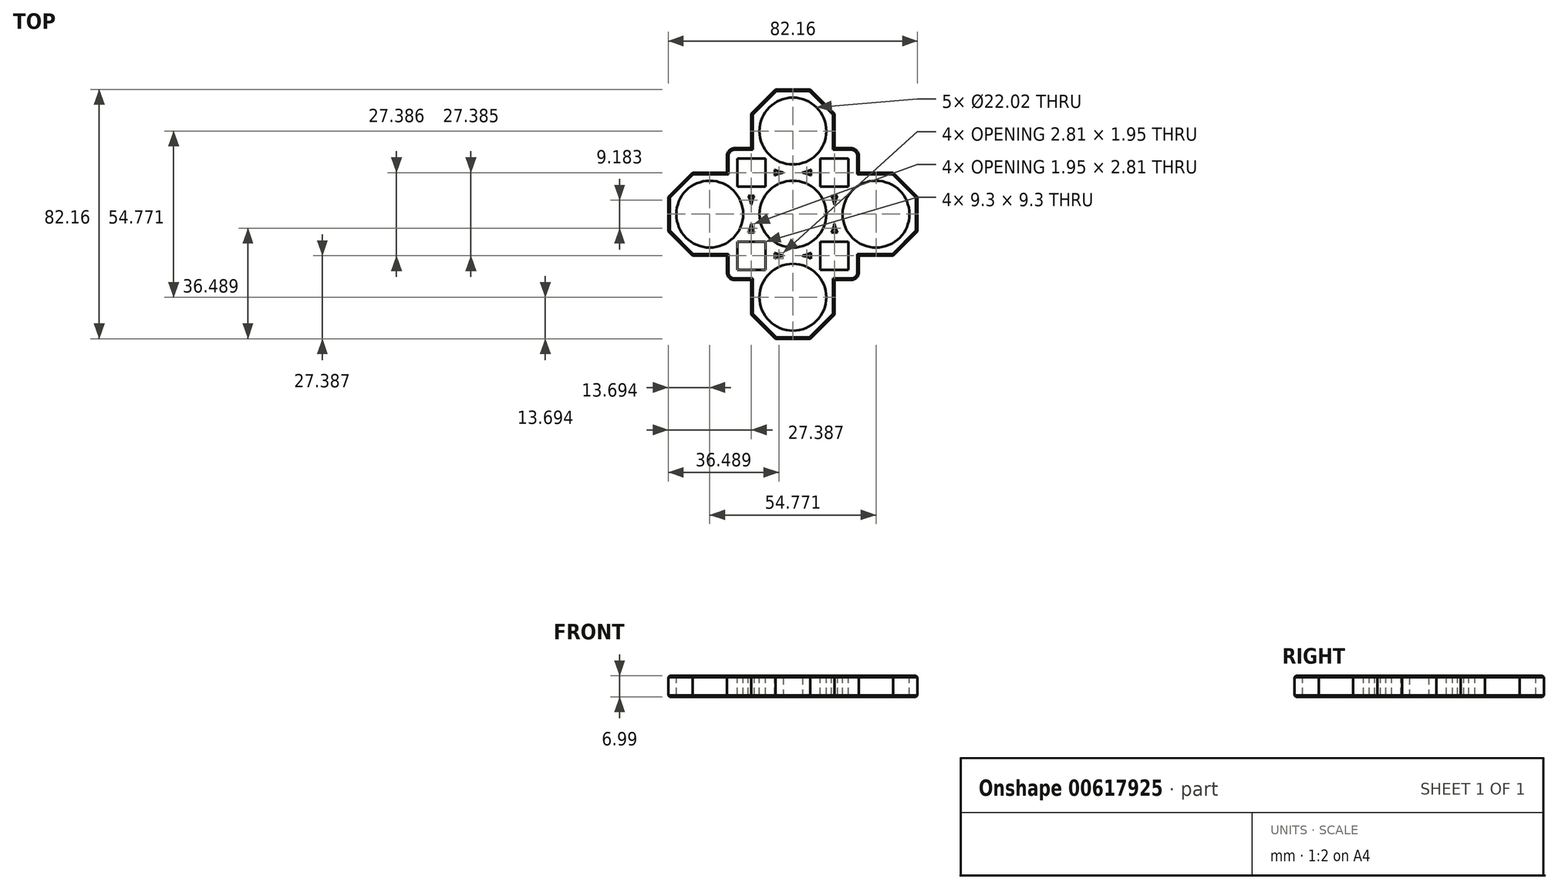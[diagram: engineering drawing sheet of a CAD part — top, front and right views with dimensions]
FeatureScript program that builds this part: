
annotation { "Feature Type Name" : "Feature", "Feature Type Description" : "" }
export const myFeature = defineFeature(function(context is Context, id is Id, definition is map)
    precondition{}
    {
        {
            var Q0;
            Q0=qCreatedBy(makeId("Top.planeOp"),FACE);
            var sketch = newSketch(context, id + "F0", { "sketchPlane" : qUnion([Q0])});
            skCircle(sketch, "E0", {"center": v(-27.39, 0) * mm, "radius": 11.01 * mm});
            skCircle(sketch, "E1.cCircle", {"center": v(-27.39, 0) * mm, "radius": 14.82 * mm, "construction": true});
            skLineSegment(sketch, "E1.0", {"start": v(-13.7, -5.67) * mm, "end": v(-21.71, -13.7) * mm});
            skLineSegment(sketch, "E1.1", {"start": v(-21.71, -13.7) * mm, "end": v(-33.06, -13.7) * mm});
            skLineSegment(sketch, "E1.2", {"start": v(-33.06, -13.7) * mm, "end": v(-41.08, -5.67) * mm});
            skLineSegment(sketch, "E1.3", {"start": v(-41.08, -5.67) * mm, "end": v(-41.08, 5.67) * mm});
            skLineSegment(sketch, "E1.4", {"start": v(-41.08, 5.67) * mm, "end": v(-33.06, 13.7) * mm});
            skLineSegment(sketch, "E1.5", {"start": v(-33.06, 13.7) * mm, "end": v(-21.71, 13.7) * mm});
            skLineSegment(sketch, "E1.6", {"start": v(-21.71, 13.7) * mm, "end": v(-13.7, 5.67) * mm});
            skLineSegment(sketch, "E1.7", {"start": v(-13.7, 5.67) * mm, "end": v(-13.7, -5.67) * mm});
            skCircle(sketch, "E2", {"center": v(0, -27.39) * mm, "radius": 11.01 * mm});
            skCircle(sketch, "E3.cCircle", {"center": v(0, -27.39) * mm, "radius": 14.82 * mm, "construction": true});
            skLineSegment(sketch, "E3.0", {"start": v(13.7, -33.06) * mm, "end": v(5.67, -41.08) * mm});
            skLineSegment(sketch, "E3.1", {"start": v(5.67, -41.08) * mm, "end": v(-5.67, -41.08) * mm});
            skLineSegment(sketch, "E3.2", {"start": v(-5.67, -41.08) * mm, "end": v(-13.7, -33.06) * mm});
            skLineSegment(sketch, "E3.3", {"start": v(-13.7, -33.06) * mm, "end": v(-13.7, -21.71) * mm});
            skLineSegment(sketch, "E3.4", {"start": v(-13.7, -21.71) * mm, "end": v(-5.67, -13.7) * mm});
            skLineSegment(sketch, "E3.5", {"start": v(-5.67, -13.7) * mm, "end": v(5.67, -13.7) * mm});
            skLineSegment(sketch, "E3.6", {"start": v(5.67, -13.7) * mm, "end": v(13.7, -21.71) * mm});
            skLineSegment(sketch, "E3.7", {"start": v(13.7, -21.71) * mm, "end": v(13.7, -33.06) * mm});
            skCircle(sketch, "E4", {"center": v(27.39, 0) * mm, "radius": 11.01 * mm});
            skCircle(sketch, "E5.cCircle", {"center": v(27.39, 0) * mm, "radius": 14.82 * mm, "construction": true});
            skLineSegment(sketch, "E5.0", {"start": v(41.08, -5.67) * mm, "end": v(33.06, -13.7) * mm});
            skLineSegment(sketch, "E5.1", {"start": v(33.06, -13.7) * mm, "end": v(21.71, -13.7) * mm});
            skLineSegment(sketch, "E5.2", {"start": v(21.71, -13.7) * mm, "end": v(13.7, -5.67) * mm});
            skLineSegment(sketch, "E5.3", {"start": v(13.7, -5.67) * mm, "end": v(13.7, 5.67) * mm});
            skLineSegment(sketch, "E5.4", {"start": v(13.7, 5.67) * mm, "end": v(21.71, 13.7) * mm});
            skLineSegment(sketch, "E5.5", {"start": v(21.71, 13.7) * mm, "end": v(33.06, 13.7) * mm});
            skLineSegment(sketch, "E5.6", {"start": v(33.06, 13.7) * mm, "end": v(41.08, 5.67) * mm});
            skLineSegment(sketch, "E5.7", {"start": v(41.08, 5.67) * mm, "end": v(41.08, -5.67) * mm});
            skCircle(sketch, "E6", {"center": v(0, 27.39) * mm, "radius": 11.01 * mm});
            skCircle(sketch, "E7.cCircle", {"center": v(0, 27.39) * mm, "radius": 14.82 * mm, "construction": true});
            skLineSegment(sketch, "E7.0", {"start": v(13.7, 21.71) * mm, "end": v(5.67, 13.7) * mm});
            skLineSegment(sketch, "E7.1", {"start": v(5.67, 13.7) * mm, "end": v(-5.67, 13.7) * mm});
            skLineSegment(sketch, "E7.2", {"start": v(-5.67, 13.7) * mm, "end": v(-13.7, 21.71) * mm});
            skLineSegment(sketch, "E7.3", {"start": v(-13.7, 21.71) * mm, "end": v(-13.7, 33.06) * mm});
            skLineSegment(sketch, "E7.4", {"start": v(-13.7, 33.06) * mm, "end": v(-5.67, 41.08) * mm});
            skLineSegment(sketch, "E7.5", {"start": v(-5.67, 41.08) * mm, "end": v(5.67, 41.08) * mm});
            skLineSegment(sketch, "E7.6", {"start": v(5.67, 41.08) * mm, "end": v(13.7, 33.06) * mm});
            skLineSegment(sketch, "E7.7", {"start": v(13.7, 33.06) * mm, "end": v(13.7, 21.71) * mm});
            skCircle(sketch, "E8", {"center": v(0, 0) * mm, "radius": 11.01 * mm});
            skCircle(sketch, "E9.cCircle", {"center": v(0, 0) * mm, "radius": 14.82 * mm, "construction": true});
            skLineSegment(sketch, "E9.1", {"start": v(5.67, -13.7) * mm, "end": v(-5.67, -13.7) * mm});
            skLineSegment(sketch, "E9.3", {"start": v(-13.7, -5.67) * mm, "end": v(-13.7, 5.67) * mm});
            skLineSegment(sketch, "E9.5", {"start": v(-5.67, 13.7) * mm, "end": v(5.67, 13.7) * mm});
            skLineSegment(sketch, "E9.7", {"start": v(13.7, 5.67) * mm, "end": v(13.7, -5.67) * mm});
            skLineSegment(sketch, "E10.bottom", {"start": v(-13.7, 21.71) * mm, "end": v(-21.71, 21.71) * mm});
            skLineSegment(sketch, "E10.right", {"start": v(-21.71, 21.71) * mm, "end": v(-21.71, 13.7) * mm});
            skLineSegment(sketch, "E11.top", {"start": v(-21.71, -21.71) * mm, "end": v(-13.7, -21.71) * mm});
            skLineSegment(sketch, "E11.left", {"start": v(-21.71, -13.7) * mm, "end": v(-21.71, -21.71) * mm});
            skLineSegment(sketch, "E12.top", {"start": v(21.71, -21.71) * mm, "end": v(13.7, -21.71) * mm});
            skLineSegment(sketch, "E12.left", {"start": v(21.71, -13.7) * mm, "end": v(21.71, -21.71) * mm});
            skLineSegment(sketch, "E13.bottom", {"start": v(13.7, 21.71) * mm, "end": v(21.71, 21.71) * mm});
            skLineSegment(sketch, "E13.right", {"start": v(21.71, 21.71) * mm, "end": v(21.71, 13.7) * mm});
            skSolve(sketch);
        }
        {
            var Q0;
            Q0 = qSketchRegion(id + "F0", true);
            extrude(context, id + "F1", {"entities" : qUnion([Q0]), "oppositeDirection" : true, "depth" : 7 * mm, "offsetDistance" : 25.4 * mm});
        }
        {
            var Q0;
            Q0=qCreatedBy(makeId("Top.planeOp"),FACE);
            var sketch = newSketch(context, id + "F2", { "sketchPlane" : qUnion([Q0])});
            skCircle(sketch, "E14.cCircle", {"center": v(-13.7, 13.7) * mm, "radius": 4.65 * mm, "construction": true});
            skLineSegment(sketch, "E14.0", {"start": v(-18.34, 18.34) * mm, "end": v(-9.04, 18.34) * mm});
            skLineSegment(sketch, "E14.1", {"start": v(-9.04, 18.34) * mm, "end": v(-9.04, 9.04) * mm});
            skLineSegment(sketch, "E14.2", {"start": v(-9.04, 9.04) * mm, "end": v(-18.34, 9.04) * mm});
            skLineSegment(sketch, "E14.3", {"start": v(-18.34, 9.04) * mm, "end": v(-18.34, 18.34) * mm});
            skPoint(sketch, "E14.0.midPoint", {"position": v(-13.7, 18.34) * mm});
            skPoint(sketch, "E15.MirrorP", {"position": v(13.7, 18.34) * mm});
            skLineSegment(sketch, "E16.MirrorCS", {"start": v(18.34, 18.34) * mm, "end": v(9.04, 18.34) * mm});
            skLineSegment(sketch, "E17.MirrorCS", {"start": v(18.34, 9.04) * mm, "end": v(18.34, 18.34) * mm});
            skCircle(sketch, "E18.MirrorC", {"center": v(13.7, 13.7) * mm, "radius": 4.65 * mm, "construction": true});
            skLineSegment(sketch, "E19.MirrorCS", {"start": v(9.04, 9.04) * mm, "end": v(18.34, 9.04) * mm});
            skLineSegment(sketch, "E20.MirrorCS", {"start": v(9.04, 18.34) * mm, "end": v(9.04, 9.04) * mm});
            skLineSegment(sketch, "E21.MirrorCS", {"start": v(18.34, -9.04) * mm, "end": v(18.34, -18.34) * mm});
            skLineSegment(sketch, "E22.MirrorCS", {"start": v(-18.34, -9.04) * mm, "end": v(-18.34, -18.34) * mm});
            skLineSegment(sketch, "E23.MirrorCS", {"start": v(-9.04, -9.04) * mm, "end": v(-18.34, -9.04) * mm});
            skLineSegment(sketch, "E24.MirrorCS", {"start": v(-9.04, -18.34) * mm, "end": v(-9.04, -9.04) * mm});
            skLineSegment(sketch, "E25.MirrorCS", {"start": v(9.04, -9.04) * mm, "end": v(18.34, -9.04) * mm});
            skLineSegment(sketch, "E26.MirrorCS", {"start": v(-18.34, -18.34) * mm, "end": v(-9.04, -18.34) * mm});
            skLineSegment(sketch, "E27.MirrorCS", {"start": v(9.04, -18.34) * mm, "end": v(9.04, -9.04) * mm});
            skLineSegment(sketch, "E28.MirrorCS", {"start": v(18.34, -18.34) * mm, "end": v(9.04, -18.34) * mm});
            skCircle(sketch, "E29.MirrorC", {"center": v(13.7, -13.7) * mm, "radius": 4.65 * mm, "construction": true});
            skCircle(sketch, "E30.MirrorC", {"center": v(-13.7, -13.7) * mm, "radius": 4.65 * mm, "construction": true});
            skPoint(sketch, "E31.MirrorP", {"position": v(-13.7, -18.34) * mm});
            skPoint(sketch, "E32.MirrorP", {"position": v(13.7, -18.34) * mm});
            skSolve(sketch);
        }
        {
            var Q0;
            Q0 = qSketchRegion(id + "F2", true);
            extrude(context, id + "F3", {"entities" : qUnion([Q0]), "operationType" : NewBodyOperationType.REMOVE, "oppositeDirection" : true, "depth" : 25.4 * mm, "offsetDistance" : 25.4 * mm});
        }
        {
            var Q0;
            Q0=makeQuery(id+"F1.opExtrude","SWEPT_EDGE",EDGE,{"disambiguationData":[OSD([sQuery(id+"F0.wireOp",EDGE,"E10.bottom"),sQuery(id+"F0.wireOp",EDGE,"E10.right")])]});
            var Q1;
            Q1=makeQuery(id+"F1.opExtrude","SWEPT_EDGE",EDGE,{"disambiguationData":[OSD([sQuery(id+"F0.wireOp",EDGE,"E13.bottom"),sQuery(id+"F0.wireOp",EDGE,"E13.right")])]});
            var Q2;
            Q2=makeQuery(id+"F1.opExtrude","SWEPT_EDGE",EDGE,{"disambiguationData":[OSD([sQuery(id+"F0.wireOp",EDGE,"E12.top"),sQuery(id+"F0.wireOp",EDGE,"E12.left")])]});
            var Q3;
            Q3=makeQuery(id+"F1.opExtrude","SWEPT_EDGE",EDGE,{"disambiguationData":[OSD([sQuery(id+"F0.wireOp",EDGE,"E11.top"),sQuery(id+"F0.wireOp",EDGE,"E11.left")])]});
            fillet(context, id + "F4", {"entities" : qUnion([Q0, Q1, Q2, Q3]), "radius" : 2.54 * mm, "tangentPropagation" : true, "allowEdgeOverflow" : false});
        }
        {
            var Q0;
            Q0=makeQuery(id+"F1.opExtrude","CAP_EDGE",EDGE,{"disambiguationData":[OSD([sQuery(id+"F0.wireOp",EDGE,"E5.7")])],"isStart":false});
            var Q1;
            Q1=makeQuery(id+"F1.opExtrude","CAP_EDGE",EDGE,{"disambiguationData":[OSD([sQuery(id+"F0.wireOp",EDGE,"E5.6")])],"isStart":false});
            var Q2;
            Q2=makeQuery(id+"F1.opExtrude","CAP_EDGE",EDGE,{"disambiguationData":[OSD([sQuery(id+"F0.wireOp",EDGE,"E5.5")])],"isStart":false});
            var Q3;
            Q3=makeQuery(id+"F1.opExtrude","CAP_EDGE",EDGE,{"disambiguationData":[OSD([sQuery(id+"F0.wireOp",EDGE,"E13.right")])],"isStart":false});
            var Q4;
            Q4=makeQuery(id+"F1.opExtrude","CAP_EDGE",EDGE,{"disambiguationData":[OSD([sQuery(id+"F0.wireOp",EDGE,"E13.bottom")])],"isStart":false});
            var Q5;
            Q5=makeQuery(id+"F1.opExtrude","CAP_EDGE",EDGE,{"disambiguationData":[OSD([sQuery(id+"F0.wireOp",EDGE,"E7.7")])],"isStart":false});
            var Q6;
            Q6=makeQuery(id+"F1.opExtrude","CAP_EDGE",EDGE,{"disambiguationData":[OSD([sQuery(id+"F0.wireOp",EDGE,"E7.6")])],"isStart":false});
            var Q7;
            Q7=makeQuery(id+"F1.opExtrude","CAP_EDGE",EDGE,{"disambiguationData":[OSD([sQuery(id+"F0.wireOp",EDGE,"E7.5")])],"isStart":false});
            var Q8;
            Q8=makeQuery(id+"F1.opExtrude","CAP_EDGE",EDGE,{"disambiguationData":[OSD([sQuery(id+"F0.wireOp",EDGE,"E7.4")])],"isStart":false});
            var Q9;
            Q9=makeQuery(id+"F1.opExtrude","CAP_EDGE",EDGE,{"disambiguationData":[OSD([sQuery(id+"F0.wireOp",EDGE,"E7.3")])],"isStart":false});
            var Q10;
            Q10=makeQuery(id+"F1.opExtrude","CAP_EDGE",EDGE,{"disambiguationData":[OSD([sQuery(id+"F0.wireOp",EDGE,"E10.bottom")])],"isStart":false});
            var Q11;
            Q11=makeQuery(id+"F1.opExtrude","CAP_EDGE",EDGE,{"disambiguationData":[OSD([sQuery(id+"F0.wireOp",EDGE,"E5.0")])],"isStart":false});
            var Q12;
            Q12=makeQuery(id+"F1.opExtrude","CAP_EDGE",EDGE,{"disambiguationData":[OSD([sQuery(id+"F0.wireOp",EDGE,"E5.1")])],"isStart":false});
            var Q13;
            Q13=makeQuery(id+"F1.opExtrude","CAP_EDGE",EDGE,{"disambiguationData":[OSD([sQuery(id+"F0.wireOp",EDGE,"E12.left")])],"isStart":false});
            var Q14;
            Q14=makeQuery(id+"F1.opExtrude","CAP_EDGE",EDGE,{"disambiguationData":[OSD([sQuery(id+"F0.wireOp",EDGE,"E12.top")])],"isStart":false});
            var Q15;
            Q15=makeQuery(id+"F1.opExtrude","CAP_EDGE",EDGE,{"disambiguationData":[OSD([sQuery(id+"F0.wireOp",EDGE,"E3.7")])],"isStart":false});
            var Q16;
            Q16=makeQuery(id+"F1.opExtrude","CAP_EDGE",EDGE,{"disambiguationData":[OSD([sQuery(id+"F0.wireOp",EDGE,"E3.0")])],"isStart":false});
            var Q17;
            Q17=makeQuery(id+"F1.opExtrude","CAP_EDGE",EDGE,{"disambiguationData":[OSD([sQuery(id+"F0.wireOp",EDGE,"E3.1")])],"isStart":false});
            var Q18;
            Q18=makeQuery(id+"F1.opExtrude","CAP_EDGE",EDGE,{"disambiguationData":[OSD([sQuery(id+"F0.wireOp",EDGE,"E3.2")])],"isStart":false});
            var Q19;
            Q19=makeQuery(id+"F1.opExtrude","CAP_EDGE",EDGE,{"disambiguationData":[OSD([sQuery(id+"F0.wireOp",EDGE,"E3.3")])],"isStart":false});
            var Q20;
            Q20=makeQuery(id+"F1.opExtrude","CAP_EDGE",EDGE,{"disambiguationData":[OSD([sQuery(id+"F0.wireOp",EDGE,"E11.top")])],"isStart":false});
            var Q21;
            Q21=makeQuery(id+"F1.opExtrude","CAP_EDGE",EDGE,{"disambiguationData":[OSD([sQuery(id+"F0.wireOp",EDGE,"E11.left")])],"isStart":false});
            var Q22;
            Q22=makeQuery(id+"F1.opExtrude","CAP_EDGE",EDGE,{"disambiguationData":[OSD([sQuery(id+"F0.wireOp",EDGE,"E1.1")])],"isStart":false});
            var Q23;
            Q23=makeQuery(id+"F1.opExtrude","CAP_EDGE",EDGE,{"disambiguationData":[OSD([sQuery(id+"F0.wireOp",EDGE,"E1.2")])],"isStart":false});
            var Q24;
            Q24=makeQuery(id+"F1.opExtrude","CAP_EDGE",EDGE,{"disambiguationData":[OSD([sQuery(id+"F0.wireOp",EDGE,"E1.3")])],"isStart":false});
            var Q25;
            Q25=makeQuery(id+"F1.opExtrude","CAP_EDGE",EDGE,{"disambiguationData":[OSD([sQuery(id+"F0.wireOp",EDGE,"E1.4")])],"isStart":false});
            var Q26;
            Q26=makeQuery(id+"F1.opExtrude","CAP_EDGE",EDGE,{"disambiguationData":[OSD([sQuery(id+"F0.wireOp",EDGE,"E1.5")])],"isStart":false});
            var Q27;
            Q27=makeQuery(id+"F1.opExtrude","CAP_EDGE",EDGE,{"disambiguationData":[OSD([sQuery(id+"F0.wireOp",EDGE,"E10.right")])],"isStart":false});
            chamfer(context, id + "F5", {"entities" : qUnion([Q0, Q1, Q2, Q3, Q4, Q5, Q6, Q7, Q8, Q9, Q10, Q11, Q12, Q13, Q14, Q15, Q16, Q17, Q18, Q19, Q20, Q21, Q22, Q23, Q24, Q25, Q26, Q27]), "width" : 0.5 * mm, "tangentPropagation" : true});
        }
        {
            var Q0;
            Q0=makeQuery(id+"F1.opExtrude","CAP_EDGE",EDGE,{"disambiguationData":[OSD([sQuery(id+"F0.wireOp",EDGE,"E3.0")])],"isStart":true});
            var Q1;
            Q1=makeQuery(id+"F1.opExtrude","CAP_EDGE",EDGE,{"disambiguationData":[OSD([sQuery(id+"F0.wireOp",EDGE,"E3.1")])],"isStart":true});
            var Q2;
            Q2=makeQuery(id+"F1.opExtrude","CAP_EDGE",EDGE,{"disambiguationData":[OSD([sQuery(id+"F0.wireOp",EDGE,"E3.2")])],"isStart":true});
            var Q3;
            Q3=makeQuery(id+"F1.opExtrude","CAP_EDGE",EDGE,{"disambiguationData":[OSD([sQuery(id+"F0.wireOp",EDGE,"E3.3")])],"isStart":true});
            var Q4;
            Q4=makeQuery(id+"F1.opExtrude","CAP_EDGE",EDGE,{"disambiguationData":[OSD([sQuery(id+"F0.wireOp",EDGE,"E11.top")])],"isStart":true});
            var Q5;
            Q5=makeQuery(id+"F1.opExtrude","CAP_EDGE",EDGE,{"disambiguationData":[OSD([sQuery(id+"F0.wireOp",EDGE,"E11.left")])],"isStart":true});
            var Q6;
            Q6=makeQuery(id+"F1.opExtrude","CAP_EDGE",EDGE,{"disambiguationData":[OSD([sQuery(id+"F0.wireOp",EDGE,"E1.1")])],"isStart":true});
            var Q7;
            Q7=makeQuery(id+"F1.opExtrude","CAP_EDGE",EDGE,{"disambiguationData":[OSD([sQuery(id+"F0.wireOp",EDGE,"E1.2")])],"isStart":true});
            var Q8;
            Q8=makeQuery(id+"F1.opExtrude","CAP_EDGE",EDGE,{"disambiguationData":[OSD([sQuery(id+"F0.wireOp",EDGE,"E1.5")])],"isStart":true});
            var Q9;
            Q9=makeQuery(id+"F1.opExtrude","CAP_EDGE",EDGE,{"disambiguationData":[OSD([sQuery(id+"F0.wireOp",EDGE,"E1.4")])],"isStart":true});
            var Q10;
            Q10=makeQuery(id+"F1.opExtrude","CAP_EDGE",EDGE,{"disambiguationData":[OSD([sQuery(id+"F0.wireOp",EDGE,"E1.3")])],"isStart":true});
            var Q11;
            Q11=makeQuery(id+"F1.opExtrude","CAP_EDGE",EDGE,{"disambiguationData":[OSD([sQuery(id+"F0.wireOp",EDGE,"E10.right")])],"isStart":true});
            var Q12;
            Q12=makeQuery(id+"F1.opExtrude","CAP_EDGE",EDGE,{"disambiguationData":[OSD([sQuery(id+"F0.wireOp",EDGE,"E10.bottom")])],"isStart":true});
            var Q13;
            Q13=makeQuery(id+"F1.opExtrude","CAP_EDGE",EDGE,{"disambiguationData":[OSD([sQuery(id+"F0.wireOp",EDGE,"E7.3")])],"isStart":true});
            var Q14;
            Q14=makeQuery(id+"F1.opExtrude","CAP_EDGE",EDGE,{"disambiguationData":[OSD([sQuery(id+"F0.wireOp",EDGE,"E7.4")])],"isStart":true});
            var Q15;
            Q15=makeQuery(id+"F1.opExtrude","CAP_EDGE",EDGE,{"disambiguationData":[OSD([sQuery(id+"F0.wireOp",EDGE,"E7.5")])],"isStart":true});
            var Q16;
            Q16=makeQuery(id+"F1.opExtrude","CAP_EDGE",EDGE,{"disambiguationData":[OSD([sQuery(id+"F0.wireOp",EDGE,"E7.6")])],"isStart":true});
            var Q17;
            Q17=makeQuery(id+"F1.opExtrude","CAP_EDGE",EDGE,{"disambiguationData":[OSD([sQuery(id+"F0.wireOp",EDGE,"E7.7")])],"isStart":true});
            var Q18;
            Q18=makeQuery(id+"F1.opExtrude","CAP_EDGE",EDGE,{"disambiguationData":[OSD([sQuery(id+"F0.wireOp",EDGE,"E13.bottom")])],"isStart":true});
            var Q19;
            Q19=makeQuery(id+"F1.opExtrude","CAP_EDGE",EDGE,{"disambiguationData":[OSD([sQuery(id+"F0.wireOp",EDGE,"E13.right")])],"isStart":true});
            var Q20;
            Q20=makeQuery(id+"F1.opExtrude","CAP_EDGE",EDGE,{"disambiguationData":[OSD([sQuery(id+"F0.wireOp",EDGE,"E5.5")])],"isStart":true});
            var Q21;
            Q21=makeQuery(id+"F1.opExtrude","CAP_EDGE",EDGE,{"disambiguationData":[OSD([sQuery(id+"F0.wireOp",EDGE,"E5.6")])],"isStart":true});
            var Q22;
            Q22=makeQuery(id+"F1.opExtrude","CAP_EDGE",EDGE,{"disambiguationData":[OSD([sQuery(id+"F0.wireOp",EDGE,"E5.7")])],"isStart":true});
            var Q23;
            Q23=makeQuery(id+"F1.opExtrude","CAP_EDGE",EDGE,{"disambiguationData":[OSD([sQuery(id+"F0.wireOp",EDGE,"E5.0")])],"isStart":true});
            var Q24;
            Q24=makeQuery(id+"F1.opExtrude","CAP_EDGE",EDGE,{"disambiguationData":[OSD([sQuery(id+"F0.wireOp",EDGE,"E5.1")])],"isStart":true});
            var Q25;
            Q25=makeQuery(id+"F1.opExtrude","CAP_EDGE",EDGE,{"disambiguationData":[OSD([sQuery(id+"F0.wireOp",EDGE,"E12.left")])],"isStart":true});
            var Q26;
            Q26=makeQuery(id+"F1.opExtrude","CAP_EDGE",EDGE,{"disambiguationData":[OSD([sQuery(id+"F0.wireOp",EDGE,"E12.top")])],"isStart":true});
            var Q27;
            Q27=makeQuery(id+"F1.opExtrude","CAP_EDGE",EDGE,{"disambiguationData":[OSD([sQuery(id+"F0.wireOp",EDGE,"E3.7")])],"isStart":true});
            chamfer(context, id + "F6", {"entities" : qUnion([Q0, Q1, Q2, Q3, Q4, Q5, Q6, Q7, Q8, Q9, Q10, Q11, Q12, Q13, Q14, Q15, Q16, Q17, Q18, Q19, Q20, Q21, Q22, Q23, Q24, Q25, Q26, Q27]), "width" : 0.5 * mm, "tangentPropagation" : true});
        }
        {
            var Q0;
            Q0=makeQuery(id+"F1.opExtrude","CAP_FACE",FACE,{"disambiguationData":[OSD([sQuery(id+"F0.wireOp",EDGE,"E0"),sQuery(id+"F0.wireOp",EDGE,"E1.1"),sQuery(id+"F0.wireOp",EDGE,"E1.2"),sQuery(id+"F0.wireOp",EDGE,"E1.3"),sQuery(id+"F0.wireOp",EDGE,"E1.4"),sQuery(id+"F0.wireOp",EDGE,"E1.5"),sQuery(id+"F0.wireOp",EDGE,"E2"),sQuery(id+"F0.wireOp",EDGE,"E3.0"),sQuery(id+"F0.wireOp",EDGE,"E3.1"),sQuery(id+"F0.wireOp",EDGE,"E3.2"),sQuery(id+"F0.wireOp",EDGE,"E3.3"),sQuery(id+"F0.wireOp",EDGE,"E3.7"),sQuery(id+"F0.wireOp",EDGE,"E4"),sQuery(id+"F0.wireOp",EDGE,"E5.0"),sQuery(id+"F0.wireOp",EDGE,"E5.1"),sQuery(id+"F0.wireOp",EDGE,"E5.5"),sQuery(id+"F0.wireOp",EDGE,"E5.6"),sQuery(id+"F0.wireOp",EDGE,"E5.7"),sQuery(id+"F0.wireOp",EDGE,"E6"),sQuery(id+"F0.wireOp",EDGE,"E7.3"),sQuery(id+"F0.wireOp",EDGE,"E7.4"),sQuery(id+"F0.wireOp",EDGE,"E7.5"),sQuery(id+"F0.wireOp",EDGE,"E7.6"),sQuery(id+"F0.wireOp",EDGE,"E7.7"),sQuery(id+"F0.wireOp",EDGE,"E8"),sQuery(id+"F0.wireOp",EDGE,"E10.bottom"),sQuery(id+"F0.wireOp",EDGE,"E10.right"),sQuery(id+"F0.wireOp",EDGE,"E11.top"),sQuery(id+"F0.wireOp",EDGE,"E11.left"),sQuery(id+"F0.wireOp",EDGE,"E12.top"),sQuery(id+"F0.wireOp",EDGE,"E12.left"),sQuery(id+"F0.wireOp",EDGE,"E13.bottom"),sQuery(id+"F0.wireOp",EDGE,"E13.right")])],"isStart":false});
            var Q1;
            Q1=makeQuery(id+"F1.opExtrude","CAP_FACE",FACE,{"disambiguationData":[OSD([sQuery(id+"F0.wireOp",EDGE,"E0"),sQuery(id+"F0.wireOp",EDGE,"E1.1"),sQuery(id+"F0.wireOp",EDGE,"E1.2"),sQuery(id+"F0.wireOp",EDGE,"E1.3"),sQuery(id+"F0.wireOp",EDGE,"E1.4"),sQuery(id+"F0.wireOp",EDGE,"E1.5"),sQuery(id+"F0.wireOp",EDGE,"E2"),sQuery(id+"F0.wireOp",EDGE,"E3.0"),sQuery(id+"F0.wireOp",EDGE,"E3.1"),sQuery(id+"F0.wireOp",EDGE,"E3.2"),sQuery(id+"F0.wireOp",EDGE,"E3.3"),sQuery(id+"F0.wireOp",EDGE,"E3.7"),sQuery(id+"F0.wireOp",EDGE,"E4"),sQuery(id+"F0.wireOp",EDGE,"E5.0"),sQuery(id+"F0.wireOp",EDGE,"E5.1"),sQuery(id+"F0.wireOp",EDGE,"E5.5"),sQuery(id+"F0.wireOp",EDGE,"E5.6"),sQuery(id+"F0.wireOp",EDGE,"E5.7"),sQuery(id+"F0.wireOp",EDGE,"E6"),sQuery(id+"F0.wireOp",EDGE,"E7.3"),sQuery(id+"F0.wireOp",EDGE,"E7.4"),sQuery(id+"F0.wireOp",EDGE,"E7.5"),sQuery(id+"F0.wireOp",EDGE,"E7.6"),sQuery(id+"F0.wireOp",EDGE,"E7.7"),sQuery(id+"F0.wireOp",EDGE,"E8"),sQuery(id+"F0.wireOp",EDGE,"E10.bottom"),sQuery(id+"F0.wireOp",EDGE,"E10.right"),sQuery(id+"F0.wireOp",EDGE,"E11.top"),sQuery(id+"F0.wireOp",EDGE,"E11.left"),sQuery(id+"F0.wireOp",EDGE,"E12.top"),sQuery(id+"F0.wireOp",EDGE,"E12.left"),sQuery(id+"F0.wireOp",EDGE,"E13.bottom"),sQuery(id+"F0.wireOp",EDGE,"E13.right")])],"isStart":true});
            shell(context, id + "F7", {"entities" : qUnion([Q0, Q1]), "thickness" : 3.05 * mm});
        }
    });
